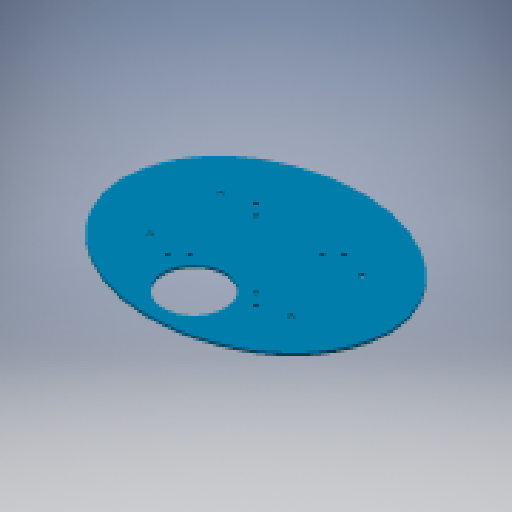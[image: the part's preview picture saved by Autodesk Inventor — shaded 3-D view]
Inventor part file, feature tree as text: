
AUTODESK INVENTOR PART (.ipt)
format: ipt  version: 2024.3 (Build 283343000, 343)  size: 157,696 bytes
history: native  units: mm
features: sketch x3, extrude x2, hole x2, other x2, reference x1
ambient origin geometry x8: Origin, YZ Plane, XZ Plane, XY Plane, X Axis, Y Axis, Z Axis, Center Point
bodies: Volumenkörper1 (feature_tree)
feature tree (10):
  extrude  "Extrusion1"  Depth=240.0mm
  hole  "Bohrung2"  [1 undecoded]
  extrude  "Extrusion3"  TaperAngle=0.0deg  [1 undecoded]
  hole  "Bohrung3"  [1 undecoded]
  sketch  "Skizze4"  dims[d0=300.0mm d1=240.0mm]
  sketch  "Skizze5"  dims[d2=3.0mm d3=0.0mm d25=80.0mm]
  reference  "Referenz2"
  sketch  "Skizze6"  dims[d26=160.0mm d27=5.2mm d28=10.0mm d29=4.0mm d30=2.0mm d31=90.0deg d32=14.2mm d33=20.594885mm d34=0.0mm d35=0.0mm d36=100.0mm d37=100.0mm d38=75.0mm d39=5.0mm d40=10.0mm d41=4.0mm d42=2.0mm d43=90.0deg d44=8.0mm d45=20.594885mm]
  other  "<path> - Kompass, Gehäuse\24_0497_0001.iam"
  other  "24_0497_0001.iam"
note: 3 required parameter values undecoded (feature->parameter linkage not recoverable at this tier; creation-order binding heuristic only, values carry confidence <= 0.55)
note: 1 file-system path scrubbed to <path> (originals preserved in map.json)
